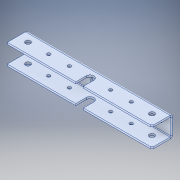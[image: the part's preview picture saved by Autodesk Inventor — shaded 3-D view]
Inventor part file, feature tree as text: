
AUTODESK INVENTOR PART (.ipt)
format: ipt  version: 2017 (Build 210142000, 142)  size: 299,008 bytes
history: native  units: in
note: dims shown in document units (in); Inventor stores cm internally (conversion verified against a paired STEP export)
features: sketch x5, hole x4, split x1, extrude x1, other x1
ambient origin geometry x8: Origin, YZ Plane, XZ Plane, XY Plane, X Axis, Y Axis, Z Axis, Center Point
bodies: Solid1 (feature_tree)
feature tree (12):
  split  "Split1"
  hole  "Hole1"  [1 undecoded]
  sketch  "Sketch3"  dims[d19=1.0in d20=0.0in]
  extrude  "Extrusion2"  Depth=0.375in
  hole  "Hole3"  [1 undecoded]
  hole  "Hole4"  [1 undecoded]
  hole  "Hole5"  [1 undecoded]
  sketch  "Sketch1"  dims[d0=0.25in d1=0.25in]
  sketch  "Sketch2"  dims[d2=0.25in d3=0.75in d4=0.375in d5=0.25in d6=0.5635in d7=1.0in d8=0.8108in d9=0.375in]
  sketch  "Sketch4"  dims[d21=0.375in d22=0.75in d23=0.375in d24=0.25in d25=0.5635in d26=1.0in d27=0.8108in d28=0.75in]
  sketch  "Sketch5"  dims[d29=0.75in d30=0.75in d31=0.375in d32=0.25in d33=0.5635in d34=1.0in d35=0.8108in d36=0.25in d37=0.25in d38=0.25in d39=0.75in d40=0.375in d41=0.25in d42=0.5635in d43=1.0in d44=0.8108in]
  other  "Break-Corner1"
note: 4 required parameter values undecoded (feature->parameter linkage not recoverable at this tier; creation-order binding heuristic only, values carry confidence <= 0.55)
